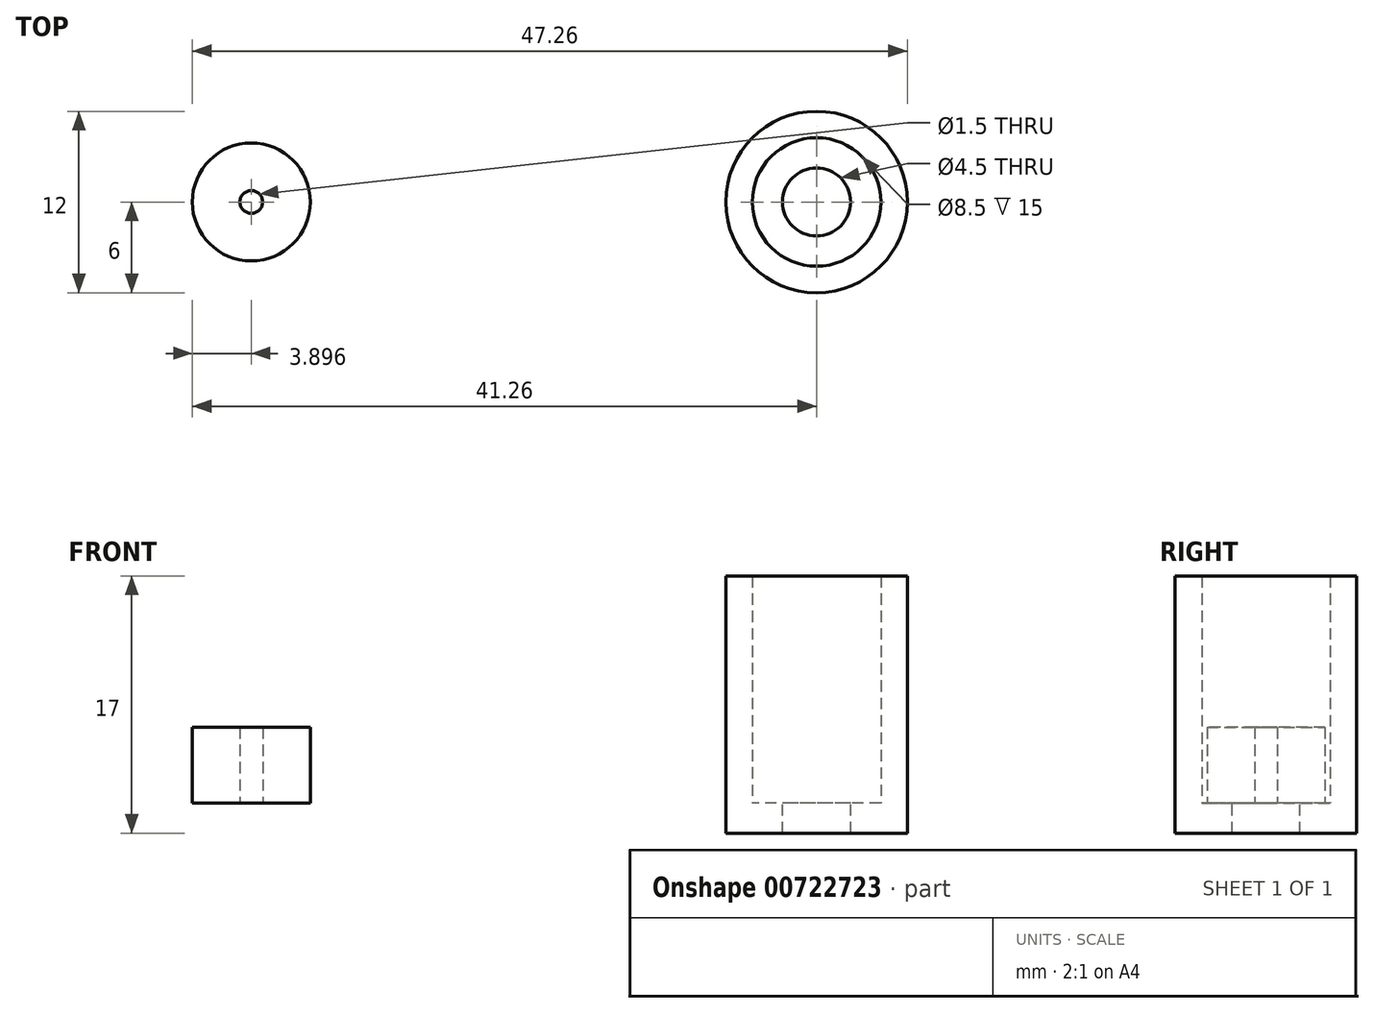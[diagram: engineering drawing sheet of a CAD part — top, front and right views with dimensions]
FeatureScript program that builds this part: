
annotation { "Feature Type Name" : "Feature", "Feature Type Description" : "" }
export const myFeature = defineFeature(function(context is Context, id is Id, definition is map)
    precondition{}
    {
        {
            var Q0;
            Q0=qCreatedBy(makeId("Top.planeOp"),FACE);
            var sketch = newSketch(context, id + "F0", { "sketchPlane" : qUnion([Q0])});
            skCircle(sketch, "E0", {"center": v(0, 0) * mm, "radius": 4.25 * mm});
            skCircle(sketch, "E1", {"center": v(0, 0) * mm, "radius": 6 * mm});
            skCircle(sketch, "E2", {"center": v(0, 0) * mm, "radius": 2.25 * mm});
            skSolve(sketch);
        }
        {
            var Q0;
            Q0=makeQuery(id+"F0.imprint","IMPRINT",FACE,{"disambiguationData":[TD([[makeQuery(id+"F0.imprint","IMPRINT",EDGE,{"derivedFrom":sQuery(id+"F0.wireOp",EDGE,"E0")}),1.0]])]});
            var Q1;
            Q1=makeQuery(id+"F0.imprint","IMPRINT",FACE,{"disambiguationData":[TD([[makeQuery(id+"F0.imprint","IMPRINT",EDGE,{"derivedFrom":sQuery(id+"F0.wireOp",EDGE,"E0")}),-1.0]])]});
            var Q2;
            Q2=sQuery(id+"F0.wireOp",EDGE,"E2");
            extrude(context, id + "F1", {"entities" : qUnion([Q0, Q1]), "surfaceEntities" : qUnion([Q2]), "oppositeDirection" : true, "depth" : 2 * mm, "offsetDistance" : 25 * mm});
        }
        {
            var Q0;
            Q0 = qSketchRegion(id + "F0", true);
            extrude(context, id + "F2", {"entities" : qUnion([Q0]), "operationType" : NewBodyOperationType.ADD, "flatOperationType" : FlatOperationType.REMOVE, "depth" : 15 * mm, "offsetDistance" : 25 * mm, "domain" : OperationDomain.MODEL});
        }
        {
            var Q0;
            Q0=qCreatedBy(makeId("Top.planeOp"),FACE);
            var sketch = newSketch(context, id + "F3", { "sketchPlane" : qUnion([Q0])});
            skCircle(sketch, "E3", {"center": v(-37.36, 0) * mm, "radius": 0.75 * mm});
            skCircle(sketch, "E4", {"center": v(-37.36, 0) * mm, "radius": 3.9 * mm});
            skSolve(sketch);
        }
        {
            var Q0;
            Q0 = qSketchRegion(id + "F3", true);
            extrude(context, id + "F4", {"entities" : qUnion([Q0]), "flatOperationType" : FlatOperationType.REMOVE, "depth" : 5 * mm, "offsetDistance" : 25 * mm, "domain" : OperationDomain.MODEL});
        }
    });
